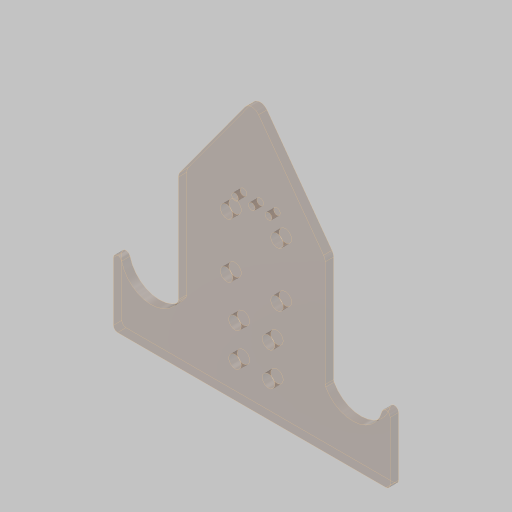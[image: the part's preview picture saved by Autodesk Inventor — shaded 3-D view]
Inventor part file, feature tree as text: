
AUTODESK INVENTOR PART (.ipt)
format: ipt  version: 2023.5 (Build 275446000, 446)  size: 371,712 bytes
history: native  units: in
note: dims shown in document units (in); Inventor stores cm internally (conversion verified against a paired STEP export)
features: sketch x5, projected_geometry x3, extrude x2, hole x2, fillet x2, mirror x1
ambient origin geometry x8: Origin, YZ Plane, XZ Plane, XY Plane, X Axis, Y Axis, Z Axis, Center Point
bodies: Solid1 (feature_tree)
feature tree (15):
  extrude  "Extrusion1"  Depth=3.0in
  hole  "Hole1"  [1 undecoded]
  fillet  "Fillet2"  Radius=5.0in
  sketch  "Sketch3"  dims[d7=0.201in d8=0.38in d9=0.385in d10=0.25in d11=0.5635in d12=1.0in d13=0.8108in d14=5.0in]
  hole  "Hole2"  [1 undecoded]
  mirror  "Mirror1"
  extrude  "Extrusion3"  Depth=0.125in
  fillet  "Fillet3"  Radius=0.75in
  sketch  "Sketch1"  dims[d0=4.375in d1=3.0in]
  sketch  "Sketch2"  dims[d2=0.25in d3=0.0in d6=1.0in]
  projected_geometry  "Projected Loop1"
  sketch  "Sketch4"  dims[d15=5.25in d16=0.25in]
  projected_geometry  "Projected Loop2"
  sketch  "Sketch5"  dims[d17=1.0in d24=0.5in d25=0.75in d26=2.125in d27=0.75in d28=0.5in d29=3.25in d30=4.25in d33=0.375in d34=0.75in d35=0.563in d36=0.12in d37=0.5635in d38=1.0in d39=0.8108in d40=6.0in d41=2.125in d42=1.3125in d43=0.25in d44=1.0in d45=0.0in d46=4.125in d48=0.125in]
  projected_geometry  "Projected Loop3"
note: 2 required parameter values undecoded (feature->parameter linkage not recoverable at this tier; creation-order binding heuristic only, values carry confidence <= 0.55)
